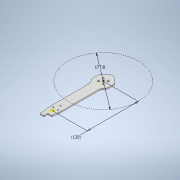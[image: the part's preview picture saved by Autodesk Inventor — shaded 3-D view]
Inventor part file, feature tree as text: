
AUTODESK INVENTOR PART (.ipt)
format: ipt  version: 2020 (Build 240168000, 168)  size: 225,792 bytes
history: native  units: in
note: dims shown in document units (in); Inventor stores cm internally (conversion verified against a paired STEP export)
features: sketch x3, extrude x2, fillet x1
ambient origin geometry x8: Origin, YZ Plane, XZ Plane, XY Plane, X Axis, Y Axis, Z Axis, Center Point
bodies: Body1 (feature_tree)
feature tree (6):
  extrude  "Extrusion1"  Depth=0.1181in
  sketch  "Sketch4"  dims[d7=0.4724in d8=5.1181in d9=7.0in]
  extrude  "Extrusion2"  Depth=5.1181in
  fillet  "Fillet1"  Radius=7.0in
  sketch  "Sketch3"  dims[d2=0.1181in d3=0.0in d4=0.8352in]
  sketch  "Sketch5"  dims[d10=5.1181in d11=0.2953in d12=0.2953in d13=0.9835in d14=0.9835in d15=0.989in d16=0.1181in d17=0.0in d18=0.3937in d19=0.3937in]
